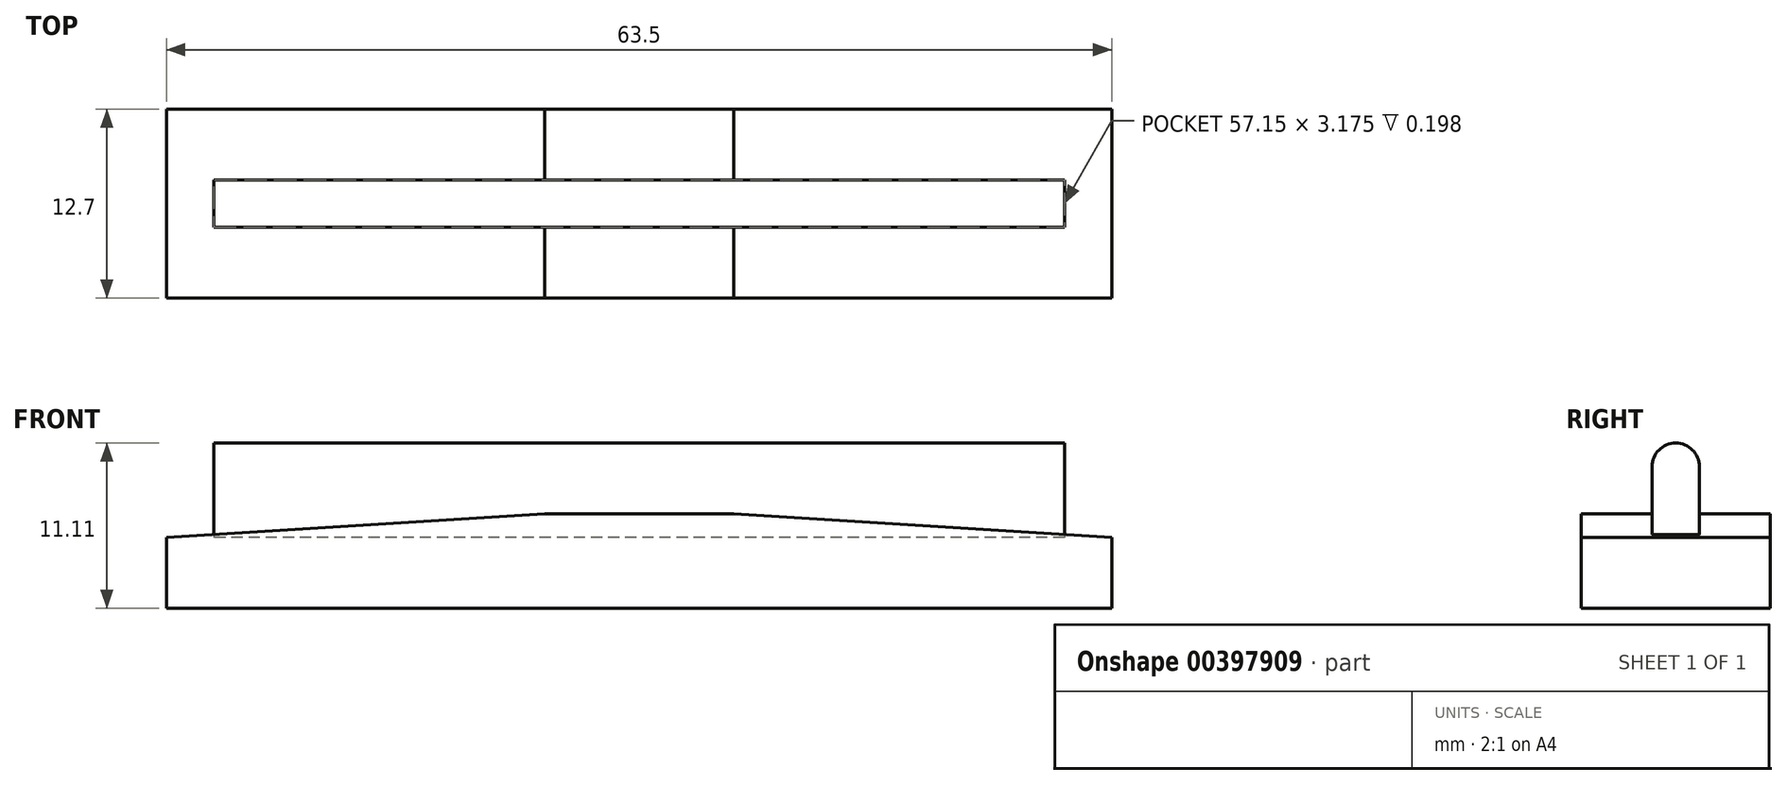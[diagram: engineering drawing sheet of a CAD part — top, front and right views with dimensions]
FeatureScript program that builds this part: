
annotation { "Feature Type Name" : "Feature", "Feature Type Description" : "" }
export const myFeature = defineFeature(function(context is Context, id is Id, definition is map)
    precondition{}
    {
        {
            var Q0;
            Q0=qCreatedBy(makeId("Top.planeOp"),FACE);
            var sketch = newSketch(context, id + "F0", { "sketchPlane" : qUnion([Q0])});
            skLineSegment(sketch, "E0.bottom", {"start": v(31.75, 6.35) * mm, "end": v(-31.75, 6.35) * mm});
            skLineSegment(sketch, "E0.top", {"start": v(31.75, -6.35) * mm, "end": v(-31.75, -6.35) * mm});
            skLineSegment(sketch, "E0.left", {"start": v(31.75, 6.35) * mm, "end": v(31.75, -6.35) * mm});
            skLineSegment(sketch, "E0.right", {"start": v(-31.75, 6.35) * mm, "end": v(-31.75, -6.35) * mm});
            skPoint(sketch, "E0.middle", {"position": v(0, 0) * mm});
            skLineSegment(sketch, "E1.bottom", {"start": v(28.58, 1.59) * mm, "end": v(-28.58, 1.59) * mm});
            skLineSegment(sketch, "E1.top", {"start": v(28.58, -1.59) * mm, "end": v(-28.58, -1.59) * mm});
            skLineSegment(sketch, "E1.left", {"start": v(28.58, 1.59) * mm, "end": v(28.58, -1.59) * mm});
            skLineSegment(sketch, "E1.right", {"start": v(-28.58, 1.59) * mm, "end": v(-28.58, -1.59) * mm});
            skSolve(sketch);
        }
        {
            var Q0;
            Q0=makeQuery(id+"F0.imprint","IMPRINT",FACE,{"disambiguationData":[TD([[makeQuery(id+"F0.imprint","IMPRINT",EDGE,{"derivedFrom":sQuery(id+"F0.wireOp",EDGE,"E0.bottom")}),1.0]])]});
            extrude(context, id + "F1", {"entities" : qUnion([Q0]), "endBound" : BoundingType.SYMMETRIC, "depth" : 3.17 * mm});
        }
        {
            var Q0;
            Q0=makeQuery(id+"F0.imprint","IMPRINT",FACE,{"disambiguationData":[TD([[makeQuery(id+"F0.imprint","IMPRINT",EDGE,{"derivedFrom":sQuery(id+"F0.wireOp",EDGE,"E1.bottom")}),1.0]])]});
            extrude(context, id + "F2", {"entities" : qUnion([Q0]), "operationType" : NewBodyOperationType.ADD, "oppositeDirection" : true, "depth" : 1.59 * mm});
        }
        {
            var Q0;
            Q0=makeQuery(id+"F0.imprint","IMPRINT",FACE,{"disambiguationData":[TD([[makeQuery(id+"F0.imprint","IMPRINT",EDGE,{"derivedFrom":sQuery(id+"F0.wireOp",EDGE,"E1.bottom")}),1.0]])]});
            extrude(context, id + "F3", {"entities" : qUnion([Q0]), "depth" : 6.35 * mm});
        }
        {
            var Q0;
            Q0=makeQuery(id+"F3.opExtrude","CAP_EDGE",EDGE,{"disambiguationData":[OSD([sQuery(id+"F0.wireOp",EDGE,"E1.top")])],"isStart":false});
            var Q1;
            Q1=makeQuery(id+"F3.opExtrude","CAP_EDGE",EDGE,{"disambiguationData":[OSD([sQuery(id+"F0.wireOp",EDGE,"E1.bottom")])],"isStart":false});
            fillet(context, id + "F4", {"entities" : qUnion([Q0, Q1]), "radius" : 1.59 * mm, "tangentPropagation" : true, "allowEdgeOverflow" : false});
        }
        {
            var Q0;
            Q0=makeQuery(id+"F1.opExtrude","CAP_EDGE",EDGE,{"disambiguationData":[OSD([sQuery(id+"F0.wireOp",EDGE,"E0.right")])],"isStart":false});
            var Q1;
            Q1=makeQuery(id+"F1.opExtrude","CAP_EDGE",EDGE,{"disambiguationData":[OSD([sQuery(id+"F0.wireOp",EDGE,"E0.left")])],"isStart":false});
            chamfer(context, id + "F5", {"entities" : qUnion([Q0, Q1]), "chamferType" : ChamferType.TWO_OFFSETS, "width1" : 25.4 * mm, "oppositeDirection" : false, "width2" : 1.59 * mm, "tangentPropagation" : true});
        }
        {
            var Q0;
            {var subQ0=sQuery(id+"F0.wireOp",EDGE,"E1.right");var subQ1=sQuery(id+"F0.wireOp",EDGE,"E1.left");var subQ2=sQuery(id+"F0.wireOp",EDGE,"E1.top");var subQ3=sQuery(id+"F0.wireOp",EDGE,"E1.bottom");Q0=makeQuery(id+"F2.boolean.opBoolean","MERGE",FACE,{"derivedFrom":[makeQuery(id+"F1.opExtrude","CAP_FACE",FACE,{"disambiguationData":[OSD([sQuery(id+"F0.wireOp",EDGE,"E0.bottom"),sQuery(id+"F0.wireOp",EDGE,"E0.top"),sQuery(id+"F0.wireOp",EDGE,"E0.left"),sQuery(id+"F0.wireOp",EDGE,"E0.right"),subQ3,subQ2,subQ1,subQ0])],"isStart":true}),makeQuery(id+"F2.opExtrude","CAP_FACE",FACE,{"disambiguationData":[OSD([subQ3,subQ2,subQ1,subQ0])],"isStart":false})]});}
            extrude(context, id + "F6", {"entities" : qUnion([Q0]), "operationType" : NewBodyOperationType.ADD, "depth" : 3.17 * mm});
        }
    });
